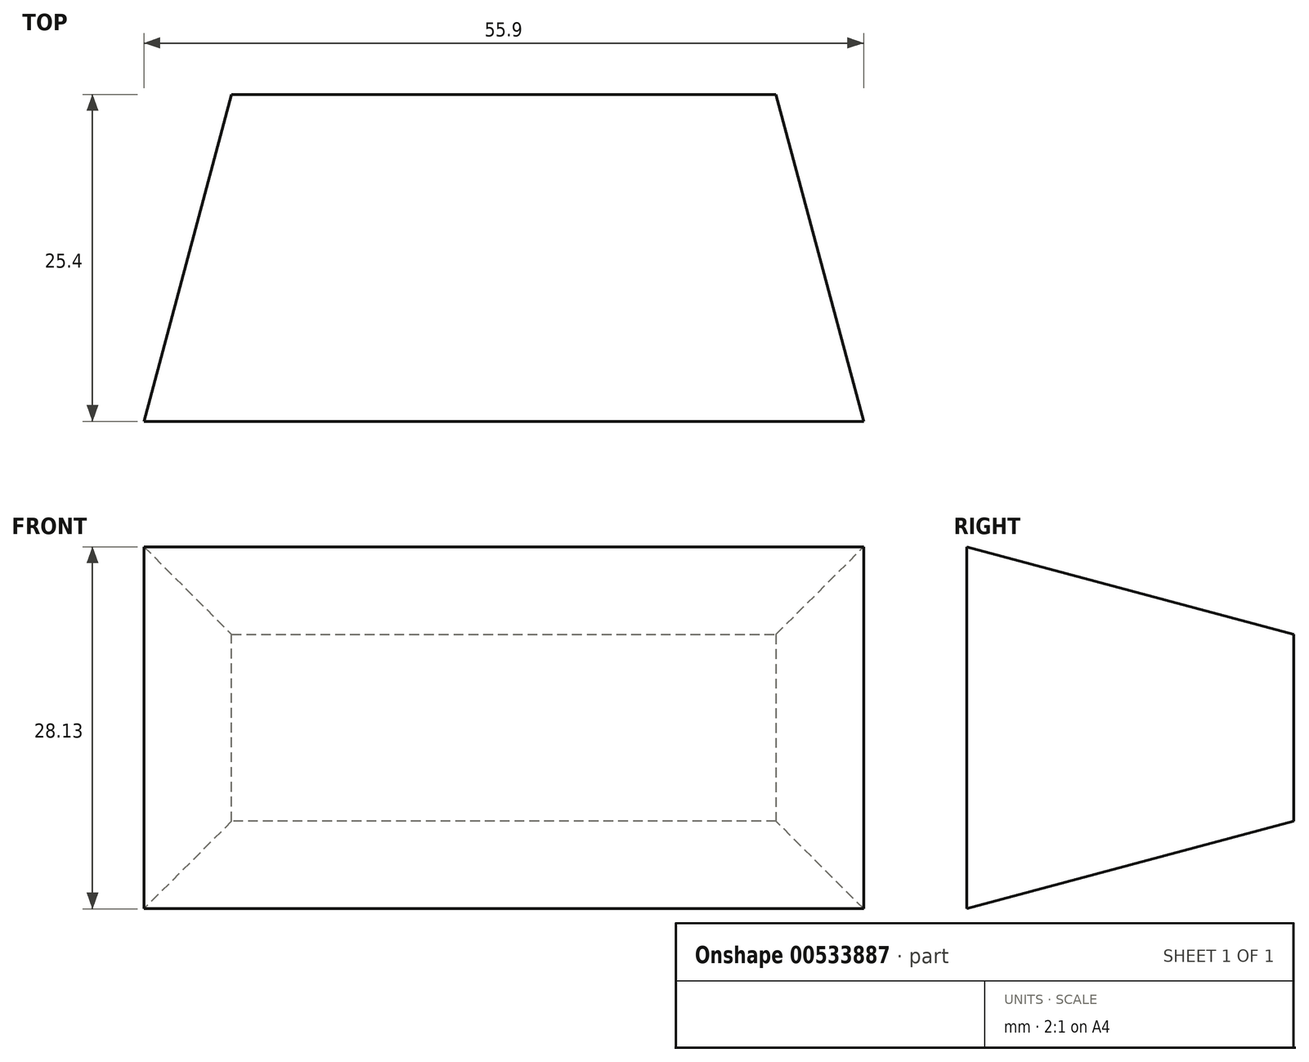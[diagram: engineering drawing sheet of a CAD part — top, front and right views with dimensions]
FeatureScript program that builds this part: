
annotation { "Feature Type Name" : "Feature", "Feature Type Description" : "" }
export const myFeature = defineFeature(function(context is Context, id is Id, definition is map)
    precondition{}
    {
        {
            var Q0;
            Q0=qCreatedBy(makeId("Front.planeOp"),FACE);
            var sketch = newSketch(context, id + "F0", { "sketchPlane" : qUnion([Q0])});
            skLineSegment(sketch, "E0.bottom", {"start": v(0, 0) * mm, "end": v(42.29, 0) * mm});
            skLineSegment(sketch, "E0.top", {"start": v(0, 14.5) * mm, "end": v(42.29, 14.5) * mm});
            skLineSegment(sketch, "E0.left", {"start": v(0, 0) * mm, "end": v(0, 14.5) * mm});
            skLineSegment(sketch, "E0.right", {"start": v(42.29, 0) * mm, "end": v(42.29, 14.5) * mm});
            skSolve(sketch);
        }
        {
            var Q0;
            Q0 = qSketchRegion(id + "F0", true);
            extrude(context, id + "F1", {"entities" : qUnion([Q0]), "depth" : 25.4 * mm, "offsetDistance" : 25.4 * mm, "hasDraft" : true, "draftAngle" : 15 * degree});
        }
    });
